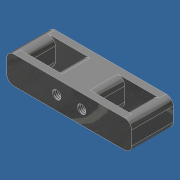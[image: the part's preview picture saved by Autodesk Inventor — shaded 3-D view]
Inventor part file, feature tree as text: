
AUTODESK INVENTOR PART (.ipt)
format: ipt  version: unknown  size: 218,624 bytes
history: native  units: in
note: dims shown in document units (in); Inventor stores cm internally (conversion verified against a paired STEP export)
features: sketch x3, extrude x2, fillet x1, hole x1
ambient origin geometry x8: Origin, YZ Plane, XZ Plane, XY Plane, X Axis, Y Axis, Z Axis, Center Point
bodies: Solid1 (feature_tree)
feature tree (7):
  extrude  "Extrusion1"  Depth=0.5in
  extrude  "Extrusion2"  Depth=0.25in
  fillet  "Fillet1"  Radius=0.5in
  hole  "Hole1"  [1 undecoded]
  sketch  "Sketch1"  dims[d0=2.25in d1=0.5in]
  sketch  "Sketch2"  dims[d2=0.75in d3=0.0in d4=0.25in d5=0.5in]
  sketch  "Sketch3"  dims[d6=0.125in d7=0.125in d8=0.25in d9=0.125in d10=0.125in d11=0.5in d12=0.75in d13=0.0in d14=0.125in d15=0.25in d16=0.25in d17=0.9in d18=0.9in d19=0.156in d20=0.75in d21=0.375in d22=0.25in d23=0.5635in d24=1.0in d25=0.8108in]
note: 1 required parameter value undecoded (feature->parameter linkage not recoverable at this tier; creation-order binding heuristic only, values carry confidence <= 0.55)
